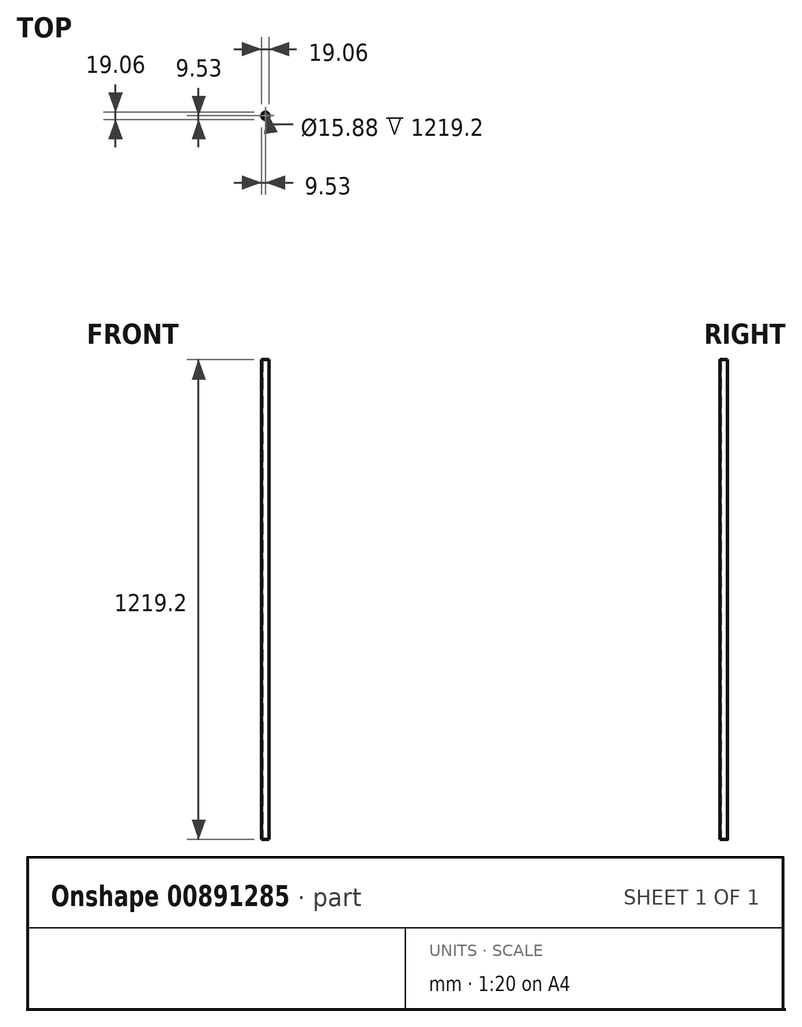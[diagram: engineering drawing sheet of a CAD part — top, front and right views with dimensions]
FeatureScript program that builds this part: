
annotation { "Feature Type Name" : "Feature", "Feature Type Description" : "" }
export const myFeature = defineFeature(function(context is Context, id is Id, definition is map)
    precondition{}
    {
        {
            var Q0;
            Q0=qCreatedBy(makeId("Top.planeOp"),FACE);
            var sketch = newSketch(context, id + "F0", { "sketchPlane" : qUnion([Q0])});
            skCircle(sketch, "E0", {"center": v(0, 0) * mm, "radius": 9.53 * mm});
            skCircle(sketch, "E1", {"center": v(0, 0) * mm, "radius": 7.94 * mm});
            skSolve(sketch);
        }
        {
            var Q0;
            Q0=qSketchRegion(id+"F0",true);
            extrude(context, id + "F1", {"entities" : qUnion([Q0]), "depth" : 1219.2 * mm, "offsetDistance" : 25.4 * mm});
        }
    });
